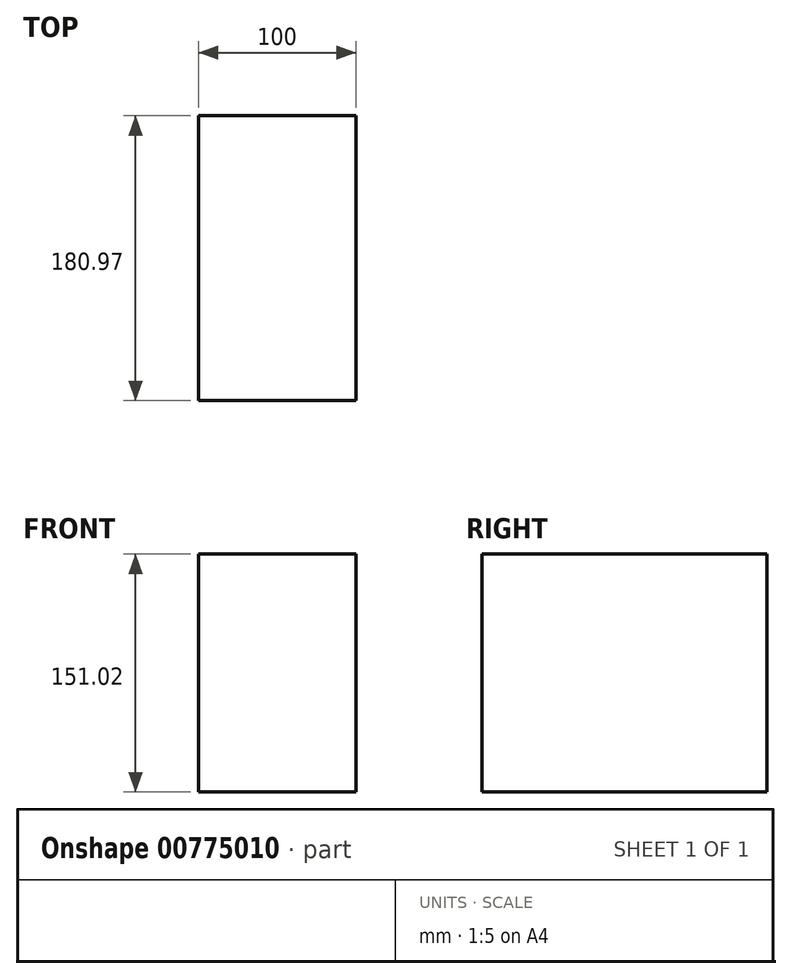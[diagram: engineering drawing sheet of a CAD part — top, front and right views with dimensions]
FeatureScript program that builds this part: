
annotation { "Feature Type Name" : "Feature", "Feature Type Description" : "" }
export const myFeature = defineFeature(function(context is Context, id is Id, definition is map)
    precondition{}
    {
        {
            var Q0;
            Q0=qCreatedBy(makeId("Right.planeOp"),FACE);
            var sketch = newSketch(context, id + "F0", { "sketchPlane" : qUnion([Q0])});
            skLineSegment(sketch, "E0.bottom", {"start": v(180.97, -132.5) * mm, "end": v(0, -132.5) * mm});
            skLineSegment(sketch, "E0.top", {"start": v(180.97, 18.52) * mm, "end": v(0, 18.52) * mm});
            skLineSegment(sketch, "E0.left", {"start": v(180.97, -132.5) * mm, "end": v(180.97, 18.52) * mm});
            skLineSegment(sketch, "E0.right", {"start": v(0, -132.5) * mm, "end": v(0, 18.52) * mm});
            skSolve(sketch);
        }
        {
            var Q0;
            Q0=makeQuery(id+"F0.imprint","IMPRINT",FACE,{"disambiguationData":[TD([[makeQuery(id+"F0.imprint","IMPRINT",EDGE,{"derivedFrom":sQuery(id+"F0.wireOp",EDGE,"E0.bottom")}),-1.0]])]});
            extrude(context, id + "F1", {"entities" : qUnion([Q0]), "depth" : 100 * mm, "offsetDistance" : 25.4 * mm});
        }
    });
